# Revit family: Electronics_Community-Point-Source_Biamp_Loudspeaker_W2_2W8
name_source: partatom
category: Communication Devices
units: mm (PartAtom-declared; Revit-internal decimal feet)

## family parameters
Cut with Voids When Loaded = No
Host = Face
Maintain Annotation Orientation = No
OmniClass Number = 23.85.10.11.14.14.14
OmniClass Title = Loudspeakers
Part Type = Normal
Room Calculation Point = No
Round Connector Dimension = Use Diameter
Shared = No

## types (4) — shared parameters
Crossover Frequency = 1 kHz
Default Elevation = 4' - 0"
Depth = 0' - 11 1/2"
Description = W2-2W8 Two-Way Dual 8-Inch Full-Range Weather-Resistant Loudspeaker
Enclosure = Hand-laminated fberglass
Environmental = IP 55W rated per IEC 60529
Finish = Black or white gelcoat
Frequency Response = 80 Hz - 15 kHz (±3 dB)
Grille = Powder-coated, zinc-plated marine grade aluminum (5052  alloy), black or white fnish (three-layer Weather-Stop™)
Height = 0' - 10"
Manufacturer = Biamp
Max Input Ratings (8 ohm) = 250W continuous, 500W program
Maximum Output = 121 dB SPL / 127 dB SPL (peak)
Minimum Impedance = 4.6 ohms @ 190 Hz
Mounting Provisions = Two (2) 1/2-13 threaded mounting points; yoke included
Nominal Beamwidth = 120° H x 60° V
Nominal Impedance = 8 ohms
Operating Range = 65 Hz to 18 kHz
Product Documentation Link = https://downloads.biamp.com
Product Page URL = https://www.biamp.com
Product data url = https://www.bimobject.com
Required Accessories = Electronic high pass flter (60 Hz, 24 dB/octave)
Sensitivity (1W/1m) = 97 dB SPL (100 Hz to 13 kHz 1/3 octave bands) 98 dB SPL (250 Hz to 4 kHz speech range)
Transducers = LF 2 x 8 (203 mm) carbon fber HF 1 x 1 (25.4 mm) exit
URL = https://www.biamp.com
Weight = 35.94 lb
Width = 1' - 8"

## per-type parameters (varying)
| type | Connector Description | Housing Material | Material Grill | Mounting Material | W2-2W8T Autoformer Taps |
| W2_2W8 B | Terminal strip; Low impedance 8 ohms | Biamp - Metal - Black | Biamp - Plastic - Black(Grid) | Biamp - Plastic - Black |  |
| W2_2W8 W | Terminal strip; Low impedance 8 ohms | Biamp - Metal - White | Biamp - Plastic - White(Grid) | Biamp - Plastic - White |  |
| W2_2W8T W | Terminal strip; 70V / 100V operation | Biamp - Metal - White | Biamp - Plastic - White(Grid) | Biamp - Plastic - White | 70V Taps - 200W, 100W, 50W, 25W; 100V Taps - 200W, 100W, 50W |
| W2_2W8T B | Terminal strip; 70V / 100V operation | Biamp - Metal - Black | Biamp - Plastic - Black(Grid) | Biamp - Plastic - Black | 70V Taps - 200W, 100W, 50W, 25W; 100V Taps - 200W, 100W, 50W |

note: column(s) folded — value = type name in every type: Model

## geometry (parser evidence)
native form markers: Sweep x4
no freeform markers — native parametric forms only
